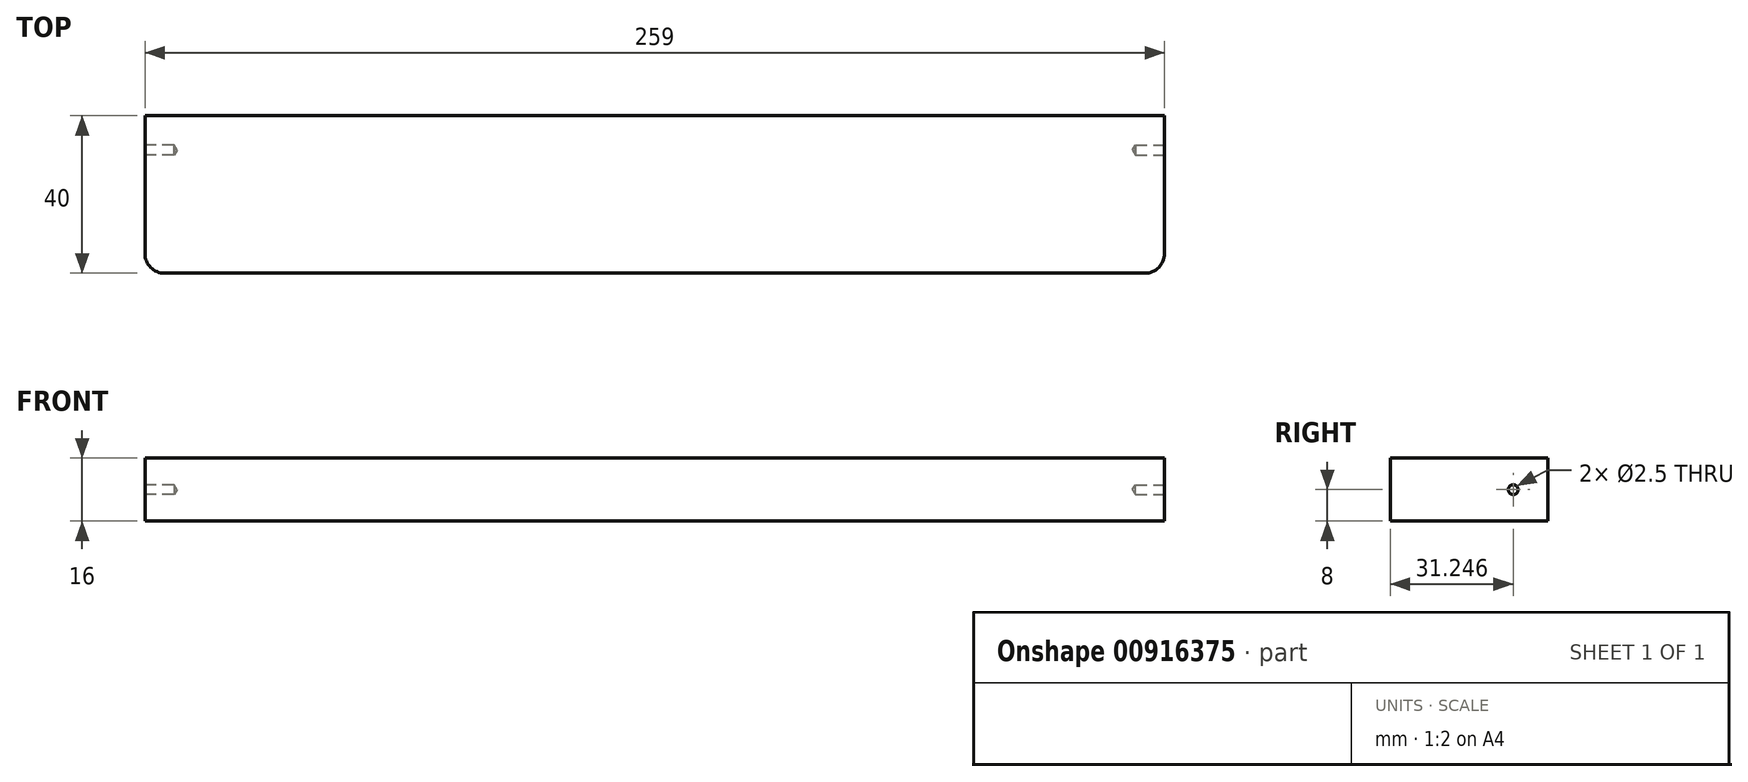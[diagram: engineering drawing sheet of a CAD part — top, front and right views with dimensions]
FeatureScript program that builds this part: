
annotation { "Feature Type Name" : "Feature", "Feature Type Description" : "" }
export const myFeature = defineFeature(function(context is Context, id is Id, definition is map)
    precondition{}
    {
        {
            var Q0;
            Q0=qCreatedBy(makeId("Top.planeOp"),FACE);
            var sketch = newSketch(context, id + "F0", { "sketchPlane" : qUnion([Q0])});
            skLineSegment(sketch, "E0.bottom", {"start": v(-85.7, -4.18) * mm, "end": v(173.3, -4.18) * mm});
            skLineSegment(sketch, "E0.top", {"start": v(-85.7, -44.18) * mm, "end": v(173.3, -44.18) * mm});
            skLineSegment(sketch, "E0.left", {"start": v(-85.7, -4.18) * mm, "end": v(-85.7, -44.18) * mm});
            skLineSegment(sketch, "E0.right", {"start": v(173.3, -4.18) * mm, "end": v(173.3, -44.18) * mm});
            skLineSegment(sketch, "E1.bottom", {"start": v(-85.7, -44.18) * mm, "end": v(-45.7, -44.18) * mm});
            skLineSegment(sketch, "E1.top", {"start": v(-85.7, -59.18) * mm, "end": v(-45.7, -59.18) * mm});
            skLineSegment(sketch, "E1.left", {"start": v(-85.7, -44.18) * mm, "end": v(-85.7, -59.18) * mm});
            skLineSegment(sketch, "E1.right", {"start": v(-45.7, -44.18) * mm, "end": v(-45.7, -59.18) * mm});
            skLineSegment(sketch, "E2.bottom", {"start": v(173.3, -44.18) * mm, "end": v(133.3, -44.18) * mm});
            skLineSegment(sketch, "E2.top", {"start": v(173.3, -59.18) * mm, "end": v(133.3, -59.18) * mm});
            skLineSegment(sketch, "E2.left", {"start": v(173.3, -44.18) * mm, "end": v(173.3, -59.18) * mm});
            skLineSegment(sketch, "E2.right", {"start": v(133.3, -44.18) * mm, "end": v(133.3, -59.18) * mm});
            skSolve(sketch);
        }
        {
            var Q0;
            Q0=makeQuery(id+"F0.imprint","IMPRINT",FACE,{"disambiguationData":[TD([[makeQuery(id+"F0.imprint","IMPRINT",EDGE,{"derivedFrom":sQuery(id+"F0.wireOp",EDGE,"E0.bottom")}),-1.0]])]});
            var Q1;
            Q1=makeQuery(id+"F0.imprint","IMPRINT",FACE,{"disambiguationData":[TD([[makeQuery(id+"F0.imprint","IMPRINT",EDGE,{"derivedFrom":sQuery(id+"F0.wireOp",EDGE,"E1.bottom")}),-1.0]])]});
            var Q2;
            Q2=makeQuery(id+"F0.imprint","IMPRINT",FACE,{"disambiguationData":[TD([[makeQuery(id+"F0.imprint","IMPRINT",EDGE,{"derivedFrom":sQuery(id+"F0.wireOp",EDGE,"E2.bottom")}),1.0]])]});
            extrude(context, id + "F1", {"entities" : qUnion([Q0, Q1, Q2]), "depth" : 16 * mm, "offsetDistance" : 25 * mm});
        }
        {
            var Q0;
            Q0=makeQuery(id+"F1.opExtrude","SWEPT_EDGE",EDGE,{"disambiguationData":[OSD([sQuery(id+"F0.wireOp",EDGE,"E1.top"),sQuery(id+"F0.wireOp",EDGE,"E1.right")])]});
            var Q1;
            Q1=makeQuery(id+"F1.opExtrude","SWEPT_EDGE",EDGE,{"disambiguationData":[OSD([sQuery(id+"F0.wireOp",EDGE,"E2.top"),sQuery(id+"F0.wireOp",EDGE,"E2.right")])]});
            var Q2;
            Q2=makeQuery(id+"F1.opExtrude","SWEPT_EDGE",EDGE,{"disambiguationData":[OSD([sQuery(id+"F0.wireOp",EDGE,"E0.top"),sQuery(id+"F0.wireOp",EDGE,"E2.bottom"),sQuery(id+"F0.wireOp",EDGE,"E2.right")])]});
            var Q3;
            Q3=makeQuery(id+"F1.opExtrude","SWEPT_EDGE",EDGE,{"disambiguationData":[OSD([sQuery(id+"F0.wireOp",EDGE,"E0.top"),sQuery(id+"F0.wireOp",EDGE,"E1.bottom"),sQuery(id+"F0.wireOp",EDGE,"E1.right")])]});
            fillet(context, id + "F2", {"entities" : qUnion([Q0, Q1, Q2, Q3]), "radius" : 5 * mm, "tangentPropagation" : true, "allowEdgeOverflow" : false});
        }
        {
            var Q0;
            Q0=makeQuery(id+"F1.opExtrude","SWEPT_FACE",FACE,{"disambiguationData":[OSD([sQuery(id+"F0.wireOp",EDGE,"E0.left"),sQuery(id+"F0.wireOp",EDGE,"E1.left")])]});
            var sketch = newSketch(context, id + "F3", { "sketchPlane" : qUnion([Q0])});
            skLineSegment(sketch, "E3", {"start": v(31.68, 0) * mm, "end": v(31.68, 8) * mm, "construction": true});
            skLineSegment(sketch, "E4", {"start": v(31.68, 8) * mm, "end": v(31.68, 16) * mm, "construction": true});
            skLineSegment(sketch, "E5", {"start": v(31.68, 8) * mm, "end": v(4.18, 8) * mm, "construction": true});
            skLineSegment(sketch, "E6", {"start": v(31.68, 8) * mm, "end": v(59.18, 8) * mm, "construction": true});
            skPoint(sketch, "E7", {"position": v(12.93, 8) * mm});
            skPoint(sketch, "E8", {"position": v(55.43, 8) * mm});
            skSolve(sketch);
        }
        {
            var Q0;
            Q0=makeQuery(id+"F1.opExtrude","SWEPT_FACE",FACE,{"disambiguationData":[OSD([sQuery(id+"F0.wireOp",EDGE,"E0.right"),sQuery(id+"F0.wireOp",EDGE,"E2.left")])]});
            var sketch = newSketch(context, id + "F4", { "sketchPlane" : qUnion([Q0])});
            skPoint(sketch, "E9", {"position": v(-55.43, 8) * mm});
            skPoint(sketch, "E10", {"position": v(-12.93, 8) * mm});
            skSolve(sketch);
        }
        {
            var Q0;
            Q0=sQuery(id+"F3.wireOp",VERTEX,"E7");
            var Q1;
            Q1=sQuery(id+"F3.wireOp",VERTEX,"E8");
            var Q2;
            Q2=sQuery(id+"F4.wireOp",VERTEX,"E10");
            var Q3;
            Q3=sQuery(id+"F4.wireOp",VERTEX,"E9");
            var Q4;
            Q4=makeQuery(id+"F1.opExtrude","SWEPT_BODY",BODY,{"disambiguationData":[OSD([sQuery(id+"F0.wireOp",EDGE,"E0.bottom"),sQuery(id+"F0.wireOp",EDGE,"E0.top"),sQuery(id+"F0.wireOp",EDGE,"E0.left"),sQuery(id+"F0.wireOp",EDGE,"E0.right"),sQuery(id+"F0.wireOp",EDGE,"E1.top"),sQuery(id+"F0.wireOp",EDGE,"E1.left"),sQuery(id+"F0.wireOp",EDGE,"E1.right"),sQuery(id+"F0.wireOp",EDGE,"E2.top"),sQuery(id+"F0.wireOp",EDGE,"E2.left"),sQuery(id+"F0.wireOp",EDGE,"E2.right")])]});
            hole(context, id + "F5", {"style" : HoleStyle.SIMPLE, "endStyle" : HoleEndStyle.BLIND, "standardTappedOrClearance" : lookupTablePath({ "standard" : "ISO", "size" : "2.5", "type" : "Drilled" }), "standardBlindInLast" : lookupTablePath({ "standard" : "ISO", "size" : "2.5", "type" : "Drilled" }), "holeDiameter" : 2.5 * mm, "majorDiameter" : 5 * mm, "holeDepth" : 7.4 * mm, "tappedDepth" : 5.3 * mm, "tapClearance" : 3, "locations" : qUnion([Q0, Q1, Q2, Q3]), "scope" : qUnion([Q4])});
        }
    });
